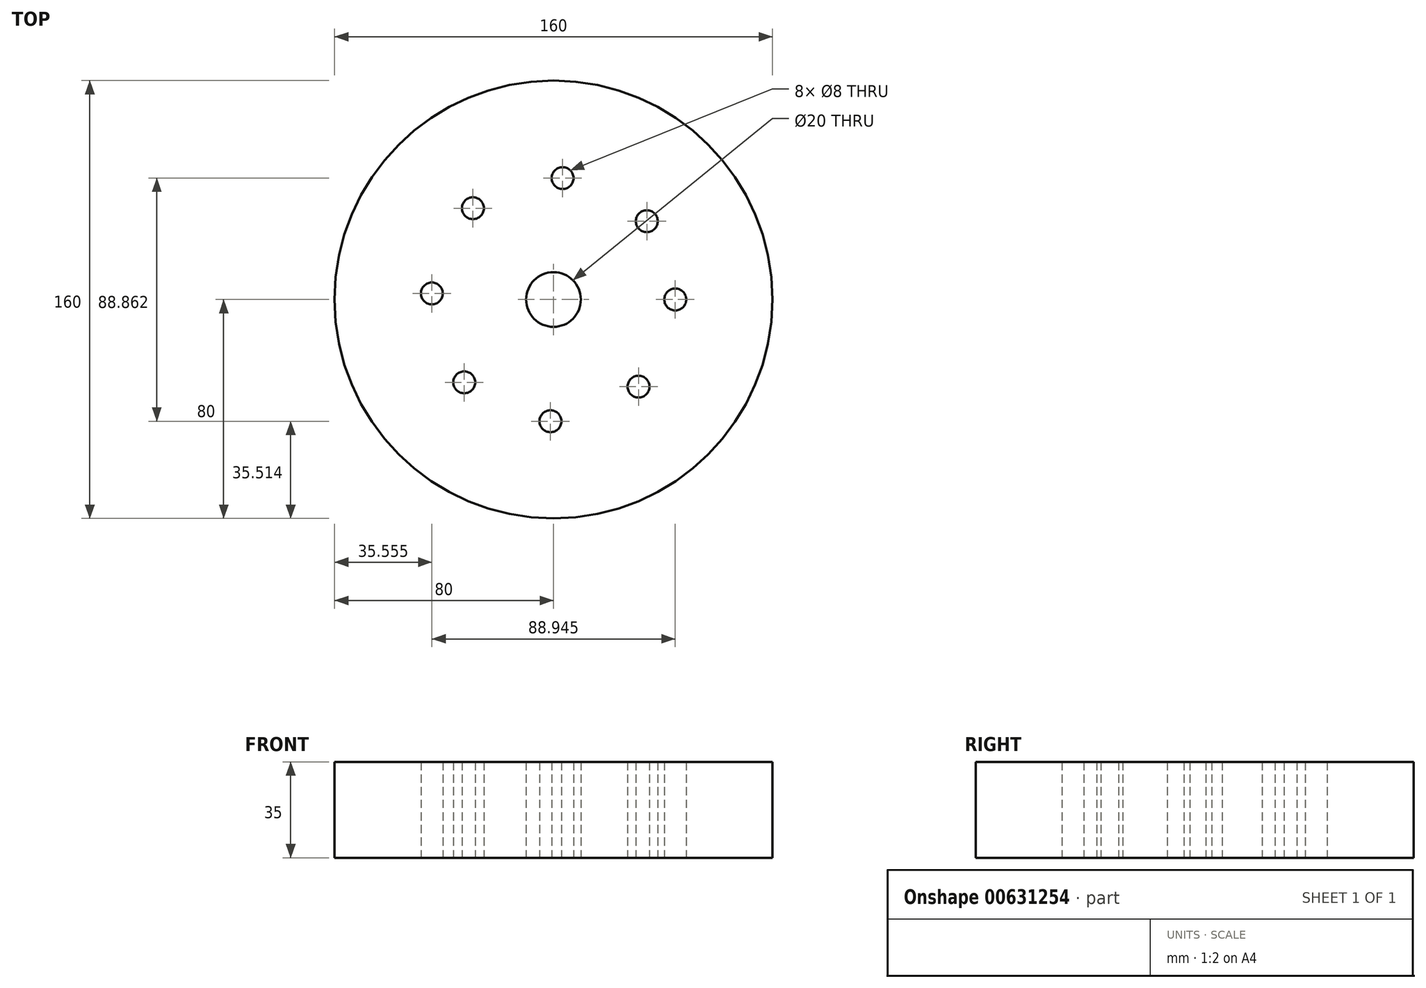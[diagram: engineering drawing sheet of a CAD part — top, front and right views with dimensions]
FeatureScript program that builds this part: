
annotation { "Feature Type Name" : "Feature", "Feature Type Description" : "" }
export const myFeature = defineFeature(function(context is Context, id is Id, definition is map)
    precondition{}
    {
        {
            var Q0;
            Q0=qCreatedBy(makeId("Top.planeOp"),FACE);
            var sketch = newSketch(context, id + "F0", { "sketchPlane" : qUnion([Q0])});
            skCircle(sketch, "E0", {"center": v(0, 0) * mm, "radius": 80 * mm});
            skSolve(sketch);
        }
        {
            var Q0;
            Q0=makeQuery(id+"F0.imprint","IMPRINT",FACE,{"disambiguationData":[TD([[makeQuery(id+"F0.imprint","IMPRINT",EDGE,{"derivedFrom":sQuery(id+"F0.wireOp",EDGE,"E0")}),1.0]])]});
            var sketch = newSketch(context, id + "F1", { "sketchPlane" : qUnion([Q0])});
            skCircle(sketch, "E1", {"center": v(0, 0) * mm, "radius": 10 * mm});
            skCircle(sketch, "E2", {"center": v(0, 0) * mm, "radius": 44.5 * mm});
            skCircle(sketch, "E3", {"center": v(44.5, 0) * mm, "radius": 4 * mm});
            skCircle(sketch, "E4.1.0", {"center": v(31.07, -31.86) * mm, "radius": 4 * mm});
            skCircle(sketch, "E4.2.0", {"center": v(-1.1, -44.49) * mm, "radius": 4 * mm});
            skCircle(sketch, "E4.3.0", {"center": v(-32.62, -30.27) * mm, "radius": 4 * mm});
            skCircle(sketch, "E4.4.0", {"center": v(-44.44, 2.22) * mm, "radius": 4 * mm});
            skCircle(sketch, "E4.5.0", {"center": v(-29.45, 33.37) * mm, "radius": 4 * mm});
            skCircle(sketch, "E4.6.0", {"center": v(3.33, 44.38) * mm, "radius": 4 * mm});
            skCircle(sketch, "E4.7.0", {"center": v(34.09, 28.6) * mm, "radius": 4 * mm});
            skLineSegment(sketch, "E4.anchor1", {"start": v(0, 0) * mm, "end": v(44.5, 0) * mm, "construction": true});
            skLineSegment(sketch, "E4.anchor2", {"start": v(0, 0) * mm, "end": v(34.09, 28.6) * mm, "construction": true});
            skSolve(sketch);
        }
        {
            var Q0;
            Q0=makeQuery(id+"F1.imprint","IMPRINT",FACE,{"disambiguationData":[TD([[makeQuery(id+"F1.imprint","IMPRINT",EDGE,{"derivedFrom":makeQuery(id+"F0.imprint","IMPRINT",EDGE,{"derivedFrom":sQuery(id+"F0.wireOp",EDGE,"E0")})}),1.0]])]});
            var Q1;
            Q1=makeQuery(id+"F1.imprint","IMPRINT",FACE,{"disambiguationData":[TD([[makeQuery(id+"F1.imprint","IMPRINT",EDGE,{"derivedFrom":sQuery(id+"F1.wireOp",EDGE,"E1")}),-1.0]])]});
            var Q2;
            Q2=makeQuery(id+"F1.imprint","IMPRINT",FACE,{"disambiguationData":[TD([[makeQuery(id+"F1.imprint","IMPRINT",EDGE,{"derivedFrom":makeQuery(id+"F0.imprint","IMPRINT",EDGE,{"derivedFrom":sQuery(id+"F0.wireOp",EDGE,"E0")})}),1.0]])]});
            var Q3;
            Q3=makeQuery(id+"F0.imprint","IMPRINT",FACE,{"disambiguationData":[TD([[makeQuery(id+"F0.imprint","IMPRINT",EDGE,{"derivedFrom":sQuery(id+"F0.wireOp",EDGE,"E0")}),1.0]])]});
            extrude(context, id + "F2", {"entities" : qUnion([Q0, Q1, Q2, Q3]), "depth" : 35 * mm, "offsetDistance" : 25 * mm});
        }
    });
